# Revit family: NLRS_57_ME_UN_variabel_volume_damper_vvremos_LT_Solid_Air
name_source: partatom
category: Mechanical Equipment
units: mm (PartAtom-declared; Revit-internal decimal feet)

## family parameters
Always vertical = Yes
Classification = None
Cut with Voids When Loaded = No
OmniClass Number = 23.75.00.00
OmniClass Title = Climate Control (HVAC)
Part Type = Normal
Room Calculation Point = No
Round Connector Dimension = Use Diameter
Shared = No
Work Plane-Based = No

## types (5) — shared parameters
Assembly Code = 57.00
Description = Variabel volumeregelaar, met geluiddemper
Manufacturer = Solid Air Climate Solutions
Model = VVREMOS
NLRS_C_content_datum_gewijzigd = 16-11-2022
NLRS_C_content_provider = Solid Air Climate Solutions
NLRS_C_content_versie = 3.20.00
NLRS_C_description = Variabel volumeregelaar, met geluiddemper
SACS_Data_Hidden = VVRMM
Type Comments = Minimaal 2x diameter aanstroom aanhouden
URL = https://solid-air.nl

## per-type parameters (varying)
| type | Default Elevation | SACS_Diameter |
| 100 | 0 mm  [stored 0 ft] | 100 mm  [stored 0.328084 ft] |
| 125 | 40 mm  [stored 0.131234 ft] | 125 mm  [stored 0.410105 ft] |
| 160 | 40 mm  [stored 0.131234 ft] | 160 mm  [stored 0.524934 ft] |
| 200 | 40 mm  [stored 0.131234 ft] | 200 mm  [stored 0.656168 ft] |
| 250 | 0 mm  [stored 0 ft] | 250 mm  [stored 0.82021 ft] |

note: [stored X ft] marks values corroborated as IEEE doubles in the binary element streams (Revit-internal decimal feet)

## geometry (parser evidence)
native form markers: Sweep x8
no freeform markers — native parametric forms only
